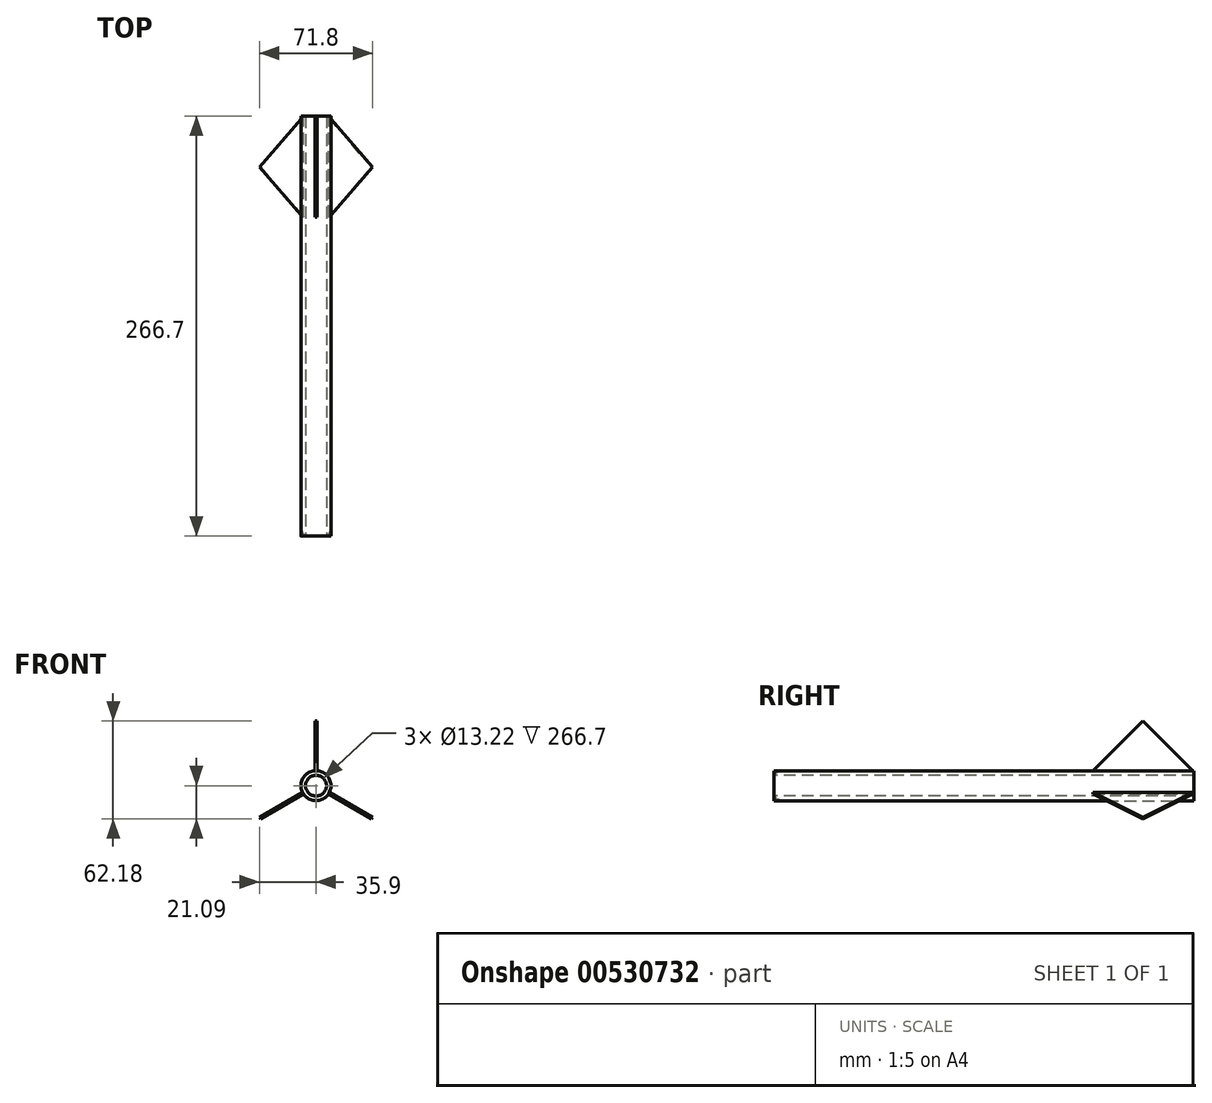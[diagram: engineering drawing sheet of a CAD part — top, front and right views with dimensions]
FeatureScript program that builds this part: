
annotation { "Feature Type Name" : "Feature", "Feature Type Description" : "" }
export const myFeature = defineFeature(function(context is Context, id is Id, definition is map)
    precondition{}
    {
        {
            var Q0;
            Q0=qCreatedBy(makeId("Front.planeOp"),FACE);
            var sketch = newSketch(context, id + "F0", { "sketchPlane" : qUnion([Q0])});
            skCircle(sketch, "E0", {"center": v(0, 0) * mm, "radius": 9.53 * mm});
            skSolve(sketch);
        }
        {
            var Q0;
            Q0=makeQuery(id+"F0.imprint","IMPRINT",FACE,{"disambiguationData":[TD([[makeQuery(id+"F0.imprint","IMPRINT",EDGE,{"derivedFrom":sQuery(id+"F0.wireOp",EDGE,"E0")}),1.0]])]});
            extrude(context, id + "F1", {"entities" : qUnion([Q0]), "endBound" : BoundingType.SYMMETRIC, "depth" : 266.7 * mm, "offsetDistance" : 25.4 * mm});
        }
        {
            var Q0;
            Q0=qCreatedBy(makeId("Front.planeOp"),FACE);
            var sketch = newSketch(context, id + "F2", { "sketchPlane" : qUnion([Q0])});
            skCircle(sketch, "E1", {"center": v(0, 0) * mm, "radius": 6.61 * mm});
            skSolve(sketch);
        }
        {
            var Q0;
            Q0=sQuery(id+"F2.wireOp",EDGE,"E1");
            extrude(context, id + "F3", {"bodyType" : ToolBodyType.SURFACE, "operationType" : NewBodyOperationType.REMOVE, "surfaceEntities" : qUnion([Q0]), "endBound" : BoundingType.SYMMETRIC, "oppositeDirection" : true, "depth" : 266.7 * mm, "offsetDistance" : 25.4 * mm});
        }
        {
            var Q0;
            Q0=qCreatedBy(makeId("Right.planeOp"),FACE);
            var sketch = newSketch(context, id + "F4", { "sketchPlane" : qUnion([Q0])});
            skLineSegment(sketch, "E2", {"start": v(132.85, 9.34) * mm, "end": v(69.1, 9.34) * mm});
            skLineSegment(sketch, "E3", {"start": v(100.97, 9.34) * mm, "end": v(100.97, 41.09) * mm});
            skLineSegment(sketch, "E4", {"start": v(100.97, 41.09) * mm, "end": v(69.1, 9.34) * mm});
            skLineSegment(sketch, "E5", {"start": v(100.97, 41.09) * mm, "end": v(132.85, 9.34) * mm});
            skSolve(sketch);
        }
        {
            var Q0;
            {var subQ2=sQuery(id+"F4.wireOp",EDGE,"E3");Q0=makeQuery(id+"F4.imprint","IMPRINT",FACE,{"disambiguationData":[TD([[makeQuery(id+"F4.imprint","IMPRINT",EDGE,{"derivedFrom":subQ2}),1.0]])]});}
            var Q1;
            {var subQ2=sQuery(id+"F4.wireOp",EDGE,"E3");Q1=makeQuery(id+"F4.imprint","IMPRINT",FACE,{"disambiguationData":[TD([[makeQuery(id+"F4.imprint","IMPRINT",EDGE,{"derivedFrom":subQ2}),-1.0]])]});}
            extrude(context, id + "F5", {"entities" : qUnion([Q0, Q1]), "operationType" : NewBodyOperationType.ADD, "endBound" : BoundingType.SYMMETRIC, "depth" : 1.27 * mm, "offsetDistance" : 25.4 * mm});
        }
        {
            var Q0;
            Q0=makeQuery(id+"F1.opExtrude","SWEPT_BODY",BODY,{"disambiguationData":[OSD([sQuery(id+"F0.wireOp",EDGE,"E0")])]});
            var Q1;
            Q1=makeQuery(id+"F1.opExtrude","CAP_EDGE",EDGE,{"disambiguationData":[OSD([sQuery(id+"F0.wireOp",EDGE,"E0")])],"isStart":true});
            transform(context, id + "F6", {"entities" : qUnion([Q0]), "transformType" : TransformType.ROTATION, "transformAxis" : qUnion([Q1]), "angle" : 120 * degree, "makeCopy" : true});
        }
        {
            var Q0;
            Q0=makeQuery(id+"F6.opPattern","COPY",BODY,{"derivedFrom":makeQuery(id+"F1.opExtrude","SWEPT_BODY",BODY,{"disambiguationData":[OSD([sQuery(id+"F0.wireOp",EDGE,"E0")])]}),"instanceName":"1"});
            var Q1;
            Q1=makeQuery(id+"F1.opExtrude","CAP_EDGE",EDGE,{"disambiguationData":[OSD([sQuery(id+"F0.wireOp",EDGE,"E0")])],"isStart":true});
            transform(context, id + "F7", {"entities" : qUnion([Q0]), "transformType" : TransformType.ROTATION, "transformAxis" : qUnion([Q1]), "angle" : 120 * degree, "makeCopy" : true});
        }
        {
            var Q0;
            Q0 = qSketchRegion(id + "F2", true);
            extrude(context, id + "F8", {"entities" : qUnion([Q0]), "operationType" : NewBodyOperationType.REMOVE, "endBound" : BoundingType.SYMMETRIC, "oppositeDirection" : true, "depth" : 266.7 * mm, "offsetDistance" : 25.4 * mm});
        }
        {
            var Q0;
            Q0=makeQuery(id+"F1.opExtrude","CAP_EDGE",EDGE,{"disambiguationData":[OSD([sQuery(id+"F0.wireOp",EDGE,"E0")])],"isStart":false});
            fillet(context, id + "F9", {"entities" : qUnion([Q0]), "radius" : 7.62 * mm, "tangentPropagation" : true, "allowEdgeOverflow" : false});
        }
    });
